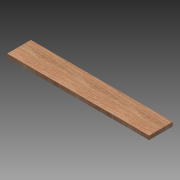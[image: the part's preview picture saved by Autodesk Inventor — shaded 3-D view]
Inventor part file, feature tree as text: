
AUTODESK INVENTOR PART (.ipt)
format: ipt  version: 2013 (Build 170138000, 138)  size: 79,360 bytes
history: native  units: in
note: dims shown in document units (in); Inventor stores cm internally (conversion verified against a paired STEP export)
features: sketch x2, extrude x1
ambient origin geometry x8: Origin, YZ Plane, XZ Plane, XY Plane, X Axis, Y Axis, Z Axis, Center Point
bodies: Solid1 (feature_tree)
feature tree (3):
  sketch  "Sketch1"  dims[d0=27.0in d1=4.5in]
  extrude  "Extrusion1"  Depth=4.5in
  sketch  "Sketch2"  dims[d2=0.75in d3=0.0in]
